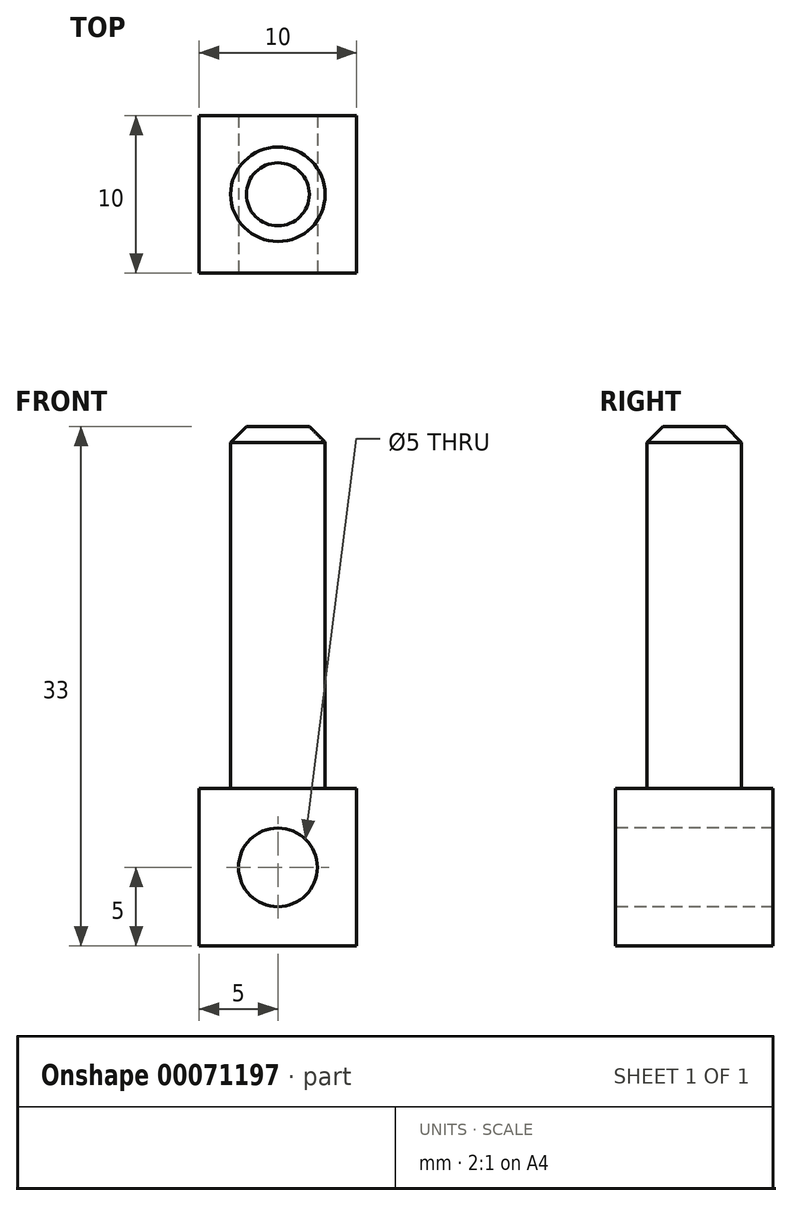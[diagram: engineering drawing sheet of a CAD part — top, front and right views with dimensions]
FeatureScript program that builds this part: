
annotation { "Feature Type Name" : "Feature", "Feature Type Description" : "" }
export const myFeature = defineFeature(function(context is Context, id is Id, definition is map)
    precondition{}
    {
        {
            var Q0;
            Q0=qCreatedBy(makeId("Top.planeOp"),FACE);
            var sketch = newSketch(context, id + "F0", { "sketchPlane" : qUnion([Q0])});
            skCircle(sketch, "E0", {"center": v(0, 0) * mm, "radius": 3 * mm});
            skLineSegment(sketch, "E1.bottom", {"start": v(-5, 5) * mm, "end": v(5, 5) * mm});
            skLineSegment(sketch, "E1.top", {"start": v(-5, -5) * mm, "end": v(5, -5) * mm});
            skLineSegment(sketch, "E1.left", {"start": v(-5, 5) * mm, "end": v(-5, -5) * mm});
            skLineSegment(sketch, "E1.right", {"start": v(5, 5) * mm, "end": v(5, -5) * mm});
            skSolve(sketch);
        }
        {
            var Q0;
            Q0=makeQuery(id+"F0.imprint","IMPRINT",FACE,{"disambiguationData":[TD([[makeQuery(id+"F0.imprint","IMPRINT",EDGE,{"derivedFrom":sQuery(id+"F0.wireOp",EDGE,"E0")}),-1.0]])]});
            extrude(context, id + "F1", {"entities" : qUnion([Q0]), "depth" : 10 * mm});
        }
        {
            var Q0;
            Q0=makeQuery(id+"F0.imprint","IMPRINT",FACE,{"disambiguationData":[TD([[makeQuery(id+"F0.imprint","IMPRINT",EDGE,{"derivedFrom":sQuery(id+"F0.wireOp",EDGE,"E0")}),1.0]])]});
            extrude(context, id + "F2", {"entities" : qUnion([Q0]), "operationType" : NewBodyOperationType.ADD, "depth" : 33 * mm});
        }
        {
            var Q0;
            Q0=makeQuery(id+"F2.opExtrude","CAP_EDGE",EDGE,{"disambiguationData":[OSD([sQuery(id+"F0.wireOp",EDGE,"E0")])],"isStart":false});
            chamfer(context, id + "F3", {"entities" : qUnion([Q0]), "width" : 1 * mm, "tangentPropagation" : true});
        }
        {
            var Q0;
            Q0=makeQuery(id+"F1.opExtrude","SWEPT_FACE",FACE,{"disambiguationData":[OSD([sQuery(id+"F0.wireOp",EDGE,"E1.top")])]});
            var sketch = newSketch(context, id + "F4", { "sketchPlane" : qUnion([Q0])});
            skCircle(sketch, "E2", {"center": v(0, 5) * mm, "radius": 2.5 * mm});
            skSolve(sketch);
        }
        {
            var Q0;
            Q0=makeQuery(id+"F4.imprint","IMPRINT",FACE,{"disambiguationData":[TD([[makeQuery(id+"F4.imprint","IMPRINT",EDGE,{"derivedFrom":sQuery(id+"F4.wireOp",EDGE,"E2")}),1.0]])]});
            extrude(context, id + "F5", {"entities" : qUnion([Q0]), "operationType" : NewBodyOperationType.REMOVE, "oppositeDirection" : true, "depth" : 25 * mm});
        }
    });
